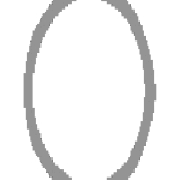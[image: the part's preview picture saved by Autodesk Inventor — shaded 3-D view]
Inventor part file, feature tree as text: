
AUTODESK INVENTOR PART (.ipt)
format: ipt  version: 2021 (Build 250183000, 183)  size: 126,976 bytes
history: native  units: in
note: dims shown in document units (in); Inventor stores cm internally (conversion verified against a paired STEP export)
features: other x4, plane x4, sketch x4, extrude x1, boolean_combine x1
ambient origin geometry x8: Origin, YZ Plane, XZ Plane, XY Plane, X Axis, Y Axis, Z Axis, Center Point
bodies: Solid1 (feature_tree), Body (feature_tree), Solid2 (feature_tree)
feature tree (14):
  other  "Driven Length"
  other  "Frame Generator"
  other  "Start Plane"
  other  "End Plane"
  plane  "Work Plane4"
  plane  "Work Plane5"
  plane  "Work Plane6"
  extrude  "Extrusion3"  Depth=0.065in
  boolean_combine  "Combine1"
  sketch  "Sketch"  dims[d5=13.5in d6=0.12in d7=0.0in d8=90.0deg d9=13.5in d10=0.12in d11=0.0in]
  sketch  "Sketch2"  dims[d0=1.0in d1=0.065in]
  plane  "Work Plane3"
  sketch  "Sketch3"  dims[d2=13.5in]
  sketch  "Sketch4"  dims[d4=-0.0in]
